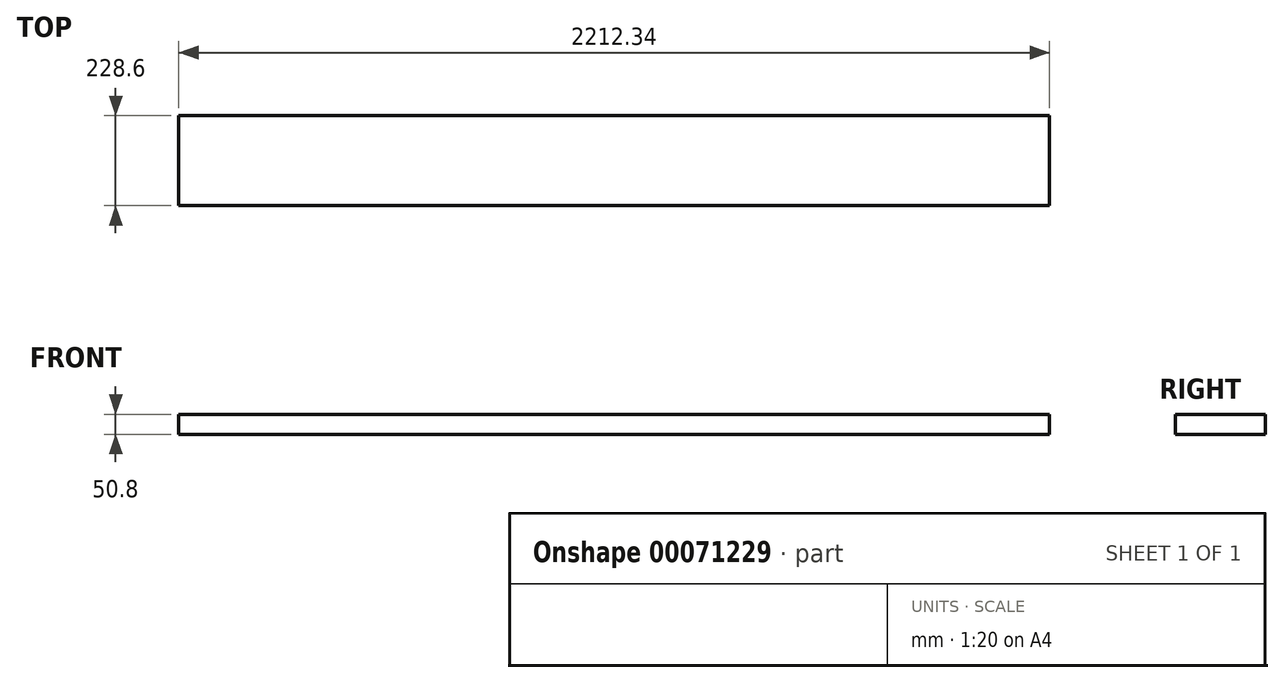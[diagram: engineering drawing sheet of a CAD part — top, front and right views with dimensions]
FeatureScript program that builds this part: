
annotation { "Feature Type Name" : "Feature", "Feature Type Description" : "" }
export const myFeature = defineFeature(function(context is Context, id is Id, definition is map)
    precondition{}
    {
        {
            var Q0;
            Q0=qCreatedBy(makeId("Front.planeOp"),FACE);
            var sketch = newSketch(context, id + "F0", { "sketchPlane" : qUnion([Q0])});
            skLineSegment(sketch, "E0.bottom", {"start": v(0, 0) * mm, "end": v(-2212.34, 0) * mm});
            skLineSegment(sketch, "E0.top", {"start": v(0, 50.8) * mm, "end": v(-2212.34, 50.8) * mm});
            skLineSegment(sketch, "E0.left", {"start": v(0, 0) * mm, "end": v(0, 50.8) * mm});
            skLineSegment(sketch, "E0.right", {"start": v(-2212.34, 0) * mm, "end": v(-2212.34, 50.8) * mm});
            skSolve(sketch);
        }
        {
            var Q0;
            Q0=makeQuery(id+"F0.imprint","IMPRINT",FACE,{"disambiguationData":[TD([[makeQuery(id+"F0.imprint","IMPRINT",EDGE,{"derivedFrom":sQuery(id+"F0.wireOp",EDGE,"E0.bottom")}),-1.0]])]});
            extrude(context, id + "F1", {"entities" : qUnion([Q0]), "depth" : 228.6 * mm});
        }
    });
